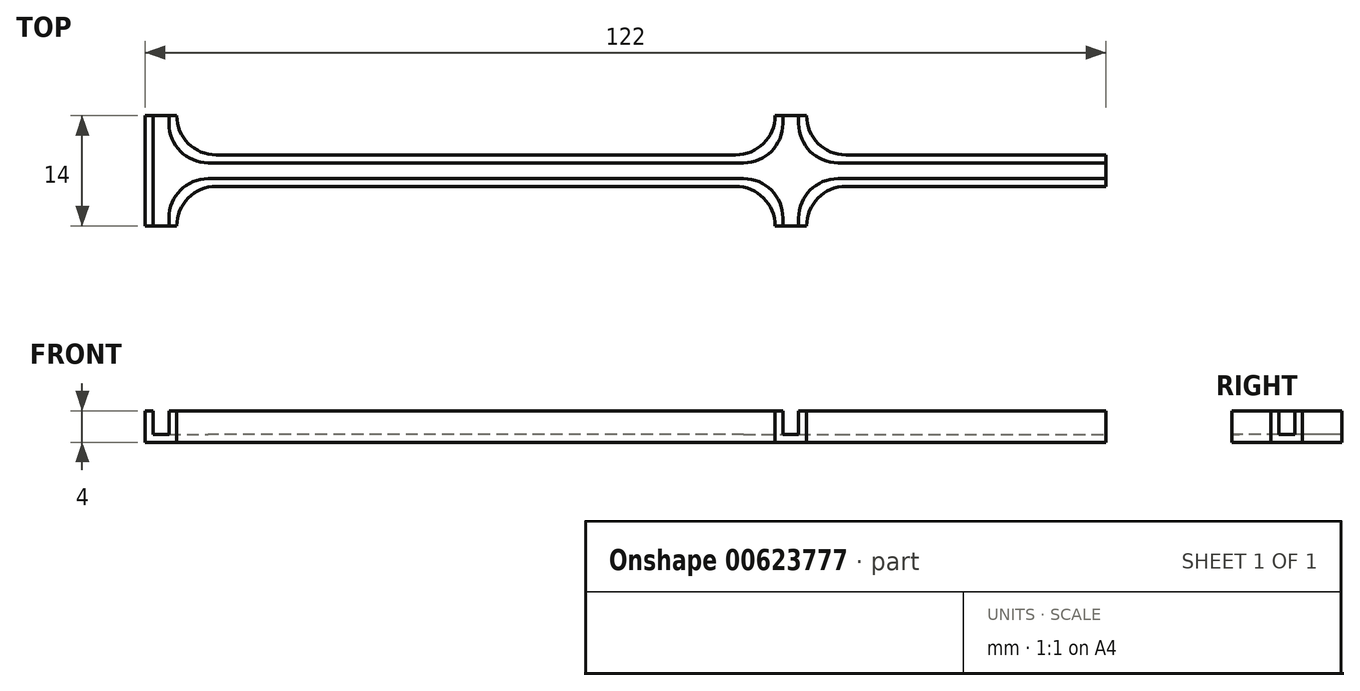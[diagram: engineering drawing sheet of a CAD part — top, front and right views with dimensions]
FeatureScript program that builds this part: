
annotation { "Feature Type Name" : "Feature", "Feature Type Description" : "" }
export const myFeature = defineFeature(function(context is Context, id is Id, definition is map)
    precondition{}
    {
        {
            var Q0;
            Q0=qCreatedBy(makeId("Top.planeOp"),FACE);
            var sketch = newSketch(context, id + "F0", { "sketchPlane" : qUnion([Q0])});
            skLineSegment(sketch, "E0.bottom", {"start": v(-61, 2) * mm, "end": v(61, 2) * mm});
            skLineSegment(sketch, "E0.top", {"start": v(-61, -2) * mm, "end": v(61, -2) * mm});
            skLineSegment(sketch, "E0.left", {"start": v(-61, 2) * mm, "end": v(-61, -2) * mm});
            skLineSegment(sketch, "E0.right", {"start": v(61, 2) * mm, "end": v(61, -2) * mm});
            skPoint(sketch, "E0.middle", {"position": v(0, 0) * mm});
            skLineSegment(sketch, "E1.bottom", {"start": v(-61, 7) * mm, "end": v(-57, 7) * mm});
            skLineSegment(sketch, "E1.top", {"start": v(-61, -7) * mm, "end": v(-57, -7) * mm});
            skLineSegment(sketch, "E1.left", {"start": v(-61, 7) * mm, "end": v(-61, -7) * mm});
            skLineSegment(sketch, "E1.right", {"start": v(-57, 7) * mm, "end": v(-57, -7) * mm});
            skLineSegment(sketch, "E2.bottom", {"start": v(-61, 0) * mm, "end": v(-61, 0) * mm});
            skLineSegment(sketch, "E2.top", {"start": v(-61, 0) * mm, "end": v(-61, 0) * mm});
            skLineSegment(sketch, "E2.left", {"start": v(-61, 0) * mm, "end": v(-61, 0) * mm});
            skLineSegment(sketch, "E2.right", {"start": v(-61, 0) * mm, "end": v(-61, 0) * mm});
            skLineSegment(sketch, "E3.bottom", {"start": v(19, 7) * mm, "end": v(23, 7) * mm});
            skLineSegment(sketch, "E3.top", {"start": v(19, -7) * mm, "end": v(23, -7) * mm});
            skLineSegment(sketch, "E3.left", {"start": v(23, 7) * mm, "end": v(23, -7) * mm});
            skLineSegment(sketch, "E3.right", {"start": v(19, 7) * mm, "end": v(19, -7) * mm});
            skLineSegment(sketch, "E4", {"start": v(-61, 0) * mm, "end": v(23, 0) * mm});
            skSolve(sketch);
        }
        {
            var Q0;
            {var subQ5=sQuery(id+"F0.wireOp",EDGE,"E1.bottom");Q0=makeQuery(id+"F0.imprint","IMPRINT",FACE,{"disambiguationData":[TD([[makeQuery(id+"F0.imprint","IMPRINT",EDGE,{"derivedFrom":subQ5}),-1.0]])]});}
            var Q1;
            {var subQ0=sQuery(id+"F0.wireOp",EDGE,"E1.right");var subQ1=sQuery(id+"F0.wireOp",EDGE,"E0.top");var subQ2=makeQuery(id+"F0.imprint","INTERSECT",VERTEX,{"derivedFrom":[subQ1,subQ0]});Q1=makeQuery(id+"F0.imprint","IMPRINT",FACE,{"disambiguationData":[TD([[makeQuery(id+"F0.imprint","IMPRINT",EDGE,{"disambiguationData":[TD([[subQ2,-1.0]])],"derivedFrom":subQ1}),1.0]])]});}
            var Q2;
            {var subQ0=sQuery(id+"F0.wireOp",EDGE,"E1.right");var subQ1=sQuery(id+"F0.wireOp",EDGE,"E0.bottom");var subQ2=makeQuery(id+"F0.imprint","INTERSECT",VERTEX,{"derivedFrom":[subQ1,subQ0]});Q2=makeQuery(id+"F0.imprint","IMPRINT",FACE,{"disambiguationData":[TD([[makeQuery(id+"F0.imprint","IMPRINT",EDGE,{"disambiguationData":[TD([[subQ2,-1.0]])],"derivedFrom":subQ1}),-1.0]])]});}
            var Q3;
            {var subQ0=sQuery(id+"F0.wireOp",EDGE,"E1.left");var subQ1=sQuery(id+"F0.wireOp",EDGE,"E0.top");var subQ2=makeQuery(id+"F0.imprint","INTERSECT",VERTEX,{"derivedFrom":[subQ1,subQ0]});Q3=makeQuery(id+"F0.imprint","IMPRINT",FACE,{"disambiguationData":[TD([[makeQuery(id+"F0.imprint","IMPRINT",EDGE,{"disambiguationData":[TD([[subQ2,-1.0]])],"derivedFrom":subQ1}),1.0]])]});}
            var Q4;
            {var subQ0=sQuery(id+"F0.wireOp",EDGE,"E1.left");var subQ1=sQuery(id+"F0.wireOp",EDGE,"E0.bottom");var subQ2=makeQuery(id+"F0.imprint","INTERSECT",VERTEX,{"derivedFrom":[subQ1,subQ0]});Q4=makeQuery(id+"F0.imprint","IMPRINT",FACE,{"disambiguationData":[TD([[makeQuery(id+"F0.imprint","IMPRINT",EDGE,{"disambiguationData":[TD([[subQ2,-1.0]])],"derivedFrom":subQ1}),-1.0]])]});}
            var Q5;
            {var subQ5=sQuery(id+"F0.wireOp",EDGE,"E1.top");Q5=makeQuery(id+"F0.imprint","IMPRINT",FACE,{"disambiguationData":[TD([[makeQuery(id+"F0.imprint","IMPRINT",EDGE,{"derivedFrom":subQ5}),1.0]])]});}
            var Q6;
            {var subQ4=sQuery(id+"F0.wireOp",EDGE,"E0.right");Q6=makeQuery(id+"F0.imprint","IMPRINT",FACE,{"disambiguationData":[TD([[makeQuery(id+"F0.imprint","IMPRINT",EDGE,{"derivedFrom":subQ4}),-1.0]])]});}
            var Q7;
            {var subQ0=sQuery(id+"F0.wireOp",EDGE,"E3.right");var subQ1=sQuery(id+"F0.wireOp",EDGE,"E0.bottom");var subQ2=makeQuery(id+"F0.imprint","INTERSECT",VERTEX,{"derivedFrom":[subQ1,subQ0]});Q7=makeQuery(id+"F0.imprint","IMPRINT",FACE,{"disambiguationData":[TD([[makeQuery(id+"F0.imprint","IMPRINT",EDGE,{"disambiguationData":[TD([[subQ2,-1.0]])],"derivedFrom":subQ1}),-1.0]])]});}
            var Q8;
            {var subQ0=sQuery(id+"F0.wireOp",EDGE,"E3.right");var subQ1=sQuery(id+"F0.wireOp",EDGE,"E0.top");var subQ2=makeQuery(id+"F0.imprint","INTERSECT",VERTEX,{"derivedFrom":[subQ1,subQ0]});Q8=makeQuery(id+"F0.imprint","IMPRINT",FACE,{"disambiguationData":[TD([[makeQuery(id+"F0.imprint","IMPRINT",EDGE,{"disambiguationData":[TD([[subQ2,-1.0]])],"derivedFrom":subQ1}),1.0]])]});}
            var Q9;
            {var subQ5=sQuery(id+"F0.wireOp",EDGE,"E3.bottom");Q9=makeQuery(id+"F0.imprint","IMPRINT",FACE,{"disambiguationData":[TD([[makeQuery(id+"F0.imprint","IMPRINT",EDGE,{"derivedFrom":subQ5}),-1.0]])]});}
            var Q10;
            {var subQ5=sQuery(id+"F0.wireOp",EDGE,"E3.top");Q10=makeQuery(id+"F0.imprint","IMPRINT",FACE,{"disambiguationData":[TD([[makeQuery(id+"F0.imprint","IMPRINT",EDGE,{"derivedFrom":subQ5}),1.0]])]});}
            extrude(context, id + "F1", {"entities" : qUnion([Q0, Q1, Q2, Q3, Q4, Q5, Q6, Q7, Q8, Q9, Q10]), "depth" : 1 * mm, "offsetDistance" : 25 * mm});
        }
        {
            var Q0;
            Q0=makeQuery(id+"F1.opExtrude","CAP_FACE",FACE,{"disambiguationData":[OSD([sQuery(id+"F0.wireOp",EDGE,"E0.bottom"),sQuery(id+"F0.wireOp",EDGE,"E0.top"),sQuery(id+"F0.wireOp",EDGE,"E0.right"),sQuery(id+"F0.wireOp",EDGE,"E1.bottom"),sQuery(id+"F0.wireOp",EDGE,"E1.top"),sQuery(id+"F0.wireOp",EDGE,"E1.left"),sQuery(id+"F0.wireOp",EDGE,"E1.right"),sQuery(id+"F0.wireOp",EDGE,"E3.bottom"),sQuery(id+"F0.wireOp",EDGE,"E3.top"),sQuery(id+"F0.wireOp",EDGE,"E3.left"),sQuery(id+"F0.wireOp",EDGE,"E3.right")])],"isStart":false});
            var sketch = newSketch(context, id + "F2", { "sketchPlane" : qUnion([Q0])});
            skLineSegment(sketch, "E5.bottom", {"start": v(-61, 7) * mm, "end": v(-60, 7) * mm});
            skLineSegment(sketch, "E5.top", {"start": v(-61, -7) * mm, "end": v(-60, -7) * mm});
            skLineSegment(sketch, "E5.left", {"start": v(-61, 7) * mm, "end": v(-61, -7) * mm});
            skLineSegment(sketch, "E5.right", {"start": v(-60, 7) * mm, "end": v(-60, -7) * mm});
            skLineSegment(sketch, "E6.bottom", {"start": v(-57, 7) * mm, "end": v(-58, 7) * mm});
            skLineSegment(sketch, "E6.top", {"start": v(-57, 1) * mm, "end": v(-58, 1) * mm});
            skLineSegment(sketch, "E6.left", {"start": v(-57, 7) * mm, "end": v(-57, 1) * mm});
            skLineSegment(sketch, "E6.right", {"start": v(-58, 7) * mm, "end": v(-58, 1) * mm});
            skLineSegment(sketch, "E7.bottom", {"start": v(-57, -7) * mm, "end": v(-58, -7) * mm});
            skLineSegment(sketch, "E7.top", {"start": v(-57, -1) * mm, "end": v(-58, -1) * mm});
            skLineSegment(sketch, "E7.left", {"start": v(-57, -7) * mm, "end": v(-57, -1) * mm});
            skLineSegment(sketch, "E7.right", {"start": v(-58, -7) * mm, "end": v(-58, -1) * mm});
            skLineSegment(sketch, "E8.bottom", {"start": v(-57, 2) * mm, "end": v(-51, 2) * mm});
            skLineSegment(sketch, "E8.top", {"start": v(-57, 1) * mm, "end": v(-51, 1) * mm});
            skLineSegment(sketch, "E8.left", {"start": v(-57, 2) * mm, "end": v(-57, 1) * mm});
            skLineSegment(sketch, "E8.right", {"start": v(-51, 2) * mm, "end": v(-51, 1) * mm});
            skLineSegment(sketch, "E9.bottom", {"start": v(-57, -1) * mm, "end": v(-51, -1) * mm});
            skLineSegment(sketch, "E9.top", {"start": v(-57, -2) * mm, "end": v(-51, -2) * mm});
            skLineSegment(sketch, "E9.left", {"start": v(-57, -1) * mm, "end": v(-57, -2) * mm});
            skLineSegment(sketch, "E9.right", {"start": v(-51, -1) * mm, "end": v(-51, -2) * mm});
            skLineSegment(sketch, "E10.bottom", {"start": v(19, 7) * mm, "end": v(20, 7) * mm});
            skLineSegment(sketch, "E10.top", {"start": v(19, 1) * mm, "end": v(20, 1) * mm});
            skLineSegment(sketch, "E10.left", {"start": v(19, 7) * mm, "end": v(19, 1) * mm});
            skLineSegment(sketch, "E10.right", {"start": v(20, 7) * mm, "end": v(20, 1) * mm});
            skLineSegment(sketch, "E11.bottom", {"start": v(19, -7) * mm, "end": v(20, -7) * mm});
            skLineSegment(sketch, "E11.top", {"start": v(19, -1) * mm, "end": v(20, -1) * mm});
            skLineSegment(sketch, "E11.left", {"start": v(19, -7) * mm, "end": v(19, -1) * mm});
            skLineSegment(sketch, "E11.right", {"start": v(20, -7) * mm, "end": v(20, -1) * mm});
            skLineSegment(sketch, "E12.bottom", {"start": v(23, -7) * mm, "end": v(22, -7) * mm});
            skLineSegment(sketch, "E12.top", {"start": v(23, -1) * mm, "end": v(22, -1) * mm});
            skLineSegment(sketch, "E12.left", {"start": v(23, -7) * mm, "end": v(23, -1) * mm});
            skLineSegment(sketch, "E12.right", {"start": v(22, -7) * mm, "end": v(22, -1) * mm});
            skLineSegment(sketch, "E13.bottom", {"start": v(23, 7) * mm, "end": v(22, 7) * mm});
            skLineSegment(sketch, "E13.top", {"start": v(23, 1) * mm, "end": v(22, 1) * mm});
            skLineSegment(sketch, "E13.left", {"start": v(23, 7) * mm, "end": v(23, 1) * mm});
            skLineSegment(sketch, "E13.right", {"start": v(22, 7) * mm, "end": v(22, 1) * mm});
            skLineSegment(sketch, "E14.bottom", {"start": v(23, 1) * mm, "end": v(28, 1) * mm});
            skLineSegment(sketch, "E14.top", {"start": v(23, 2) * mm, "end": v(28, 2) * mm});
            skLineSegment(sketch, "E14.left", {"start": v(23, 1) * mm, "end": v(23, 2) * mm});
            skLineSegment(sketch, "E14.right", {"start": v(28, 1) * mm, "end": v(28, 2) * mm});
            skLineSegment(sketch, "E15.bottom", {"start": v(23, -1) * mm, "end": v(28, -1) * mm});
            skLineSegment(sketch, "E15.top", {"start": v(23, -2) * mm, "end": v(28, -2) * mm});
            skLineSegment(sketch, "E15.left", {"start": v(23, -1) * mm, "end": v(23, -2) * mm});
            skLineSegment(sketch, "E15.right", {"start": v(28, -1) * mm, "end": v(28, -2) * mm});
            skLineSegment(sketch, "E16.bottom", {"start": v(19, -1) * mm, "end": v(14, -1) * mm});
            skLineSegment(sketch, "E16.top", {"start": v(19, -2) * mm, "end": v(14, -2) * mm});
            skLineSegment(sketch, "E16.left", {"start": v(19, -1) * mm, "end": v(19, -2) * mm});
            skLineSegment(sketch, "E16.right", {"start": v(14, -1) * mm, "end": v(14, -2) * mm});
            skLineSegment(sketch, "E17.bottom", {"start": v(19, 1) * mm, "end": v(14, 1) * mm});
            skLineSegment(sketch, "E17.top", {"start": v(19, 2) * mm, "end": v(14, 2) * mm});
            skLineSegment(sketch, "E17.left", {"start": v(19, 1) * mm, "end": v(19, 2) * mm});
            skLineSegment(sketch, "E17.right", {"start": v(14, 1) * mm, "end": v(14, 2) * mm});
            skLineSegment(sketch, "E18.bottom", {"start": v(-51, -1) * mm, "end": v(14, -1) * mm});
            skLineSegment(sketch, "E18.top", {"start": v(-51, -2) * mm, "end": v(14, -2) * mm});
            skLineSegment(sketch, "E19.bottom", {"start": v(-51, 2) * mm, "end": v(14, 2) * mm});
            skLineSegment(sketch, "E19.top", {"start": v(-51, 1) * mm, "end": v(14, 1) * mm});
            skLineSegment(sketch, "E19.right", {"start": v(14, 2) * mm, "end": v(14, 1) * mm});
            skLineSegment(sketch, "E20.bottom", {"start": v(28, 1) * mm, "end": v(61, 1) * mm});
            skLineSegment(sketch, "E20.top", {"start": v(28, 2) * mm, "end": v(61, 2) * mm});
            skLineSegment(sketch, "E20.right", {"start": v(61, 1) * mm, "end": v(61, 2) * mm});
            skLineSegment(sketch, "E21.bottom", {"start": v(28, -1) * mm, "end": v(61, -1) * mm});
            skLineSegment(sketch, "E21.top", {"start": v(28, -2) * mm, "end": v(61, -2) * mm});
            skLineSegment(sketch, "E21.right", {"start": v(61, -1) * mm, "end": v(61, -2) * mm});
            skSolve(sketch);
        }
        {
            var Q0;
            Q0=makeQuery(id+"F2.imprint","IMPRINT",FACE,{"disambiguationData":[TD([[makeQuery(id+"F2.imprint","IMPRINT",EDGE,{"derivedFrom":sQuery(id+"F2.wireOp",EDGE,"E5.bottom")}),-1.0]])]});
            var Q1;
            Q1=makeQuery(id+"F2.imprint","IMPRINT",FACE,{"disambiguationData":[TD([[makeQuery(id+"F2.imprint","IMPRINT",EDGE,{"derivedFrom":sQuery(id+"F2.wireOp",EDGE,"E6.bottom")}),-1.0]])]});
            var Q2;
            Q2=makeQuery(id+"F2.imprint","IMPRINT",FACE,{"disambiguationData":[TD([[makeQuery(id+"F2.imprint","IMPRINT",EDGE,{"derivedFrom":sQuery(id+"F2.wireOp",EDGE,"E8.bottom")}),-1.0]])]});
            var Q3;
            Q3=makeQuery(id+"F2.imprint","IMPRINT",FACE,{"disambiguationData":[TD([[makeQuery(id+"F2.imprint","IMPRINT",EDGE,{"derivedFrom":sQuery(id+"F2.wireOp",EDGE,"E9.bottom")}),-1.0]])]});
            var Q4;
            Q4=makeQuery(id+"F2.imprint","IMPRINT",FACE,{"disambiguationData":[TD([[makeQuery(id+"F2.imprint","IMPRINT",EDGE,{"derivedFrom":sQuery(id+"F2.wireOp",EDGE,"E7.bottom")}),1.0]])]});
            var Q5;
            Q5=makeQuery(id+"F2.imprint","IMPRINT",FACE,{"disambiguationData":[TD([[makeQuery(id+"F2.imprint","IMPRINT",EDGE,{"derivedFrom":sQuery(id+"F2.wireOp",EDGE,"E11.bottom")}),1.0]])]});
            var Q6;
            Q6=makeQuery(id+"F2.imprint","IMPRINT",FACE,{"disambiguationData":[TD([[makeQuery(id+"F2.imprint","IMPRINT",EDGE,{"derivedFrom":sQuery(id+"F2.wireOp",EDGE,"E10.bottom")}),-1.0]])]});
            var Q7;
            Q7=makeQuery(id+"F2.imprint","IMPRINT",FACE,{"disambiguationData":[TD([[makeQuery(id+"F2.imprint","IMPRINT",EDGE,{"derivedFrom":sQuery(id+"F2.wireOp",EDGE,"E17.bottom")}),-1.0]])]});
            var Q8;
            Q8=makeQuery(id+"F2.imprint","IMPRINT",FACE,{"disambiguationData":[TD([[makeQuery(id+"F2.imprint","IMPRINT",EDGE,{"derivedFrom":sQuery(id+"F2.wireOp",EDGE,"E16.bottom")}),1.0]])]});
            var Q9;
            Q9=makeQuery(id+"F2.imprint","IMPRINT",FACE,{"disambiguationData":[TD([[makeQuery(id+"F2.imprint","IMPRINT",EDGE,{"derivedFrom":sQuery(id+"F2.wireOp",EDGE,"E15.bottom")}),-1.0]])]});
            var Q10;
            Q10=makeQuery(id+"F2.imprint","IMPRINT",FACE,{"disambiguationData":[TD([[makeQuery(id+"F2.imprint","IMPRINT",EDGE,{"derivedFrom":sQuery(id+"F2.wireOp",EDGE,"E14.bottom")}),1.0]])]});
            var Q11;
            Q11=makeQuery(id+"F2.imprint","IMPRINT",FACE,{"disambiguationData":[TD([[makeQuery(id+"F2.imprint","IMPRINT",EDGE,{"derivedFrom":sQuery(id+"F2.wireOp",EDGE,"E13.bottom")}),-1.0]])]});
            var Q12;
            Q12=makeQuery(id+"F2.imprint","IMPRINT",FACE,{"disambiguationData":[TD([[makeQuery(id+"F2.imprint","IMPRINT",EDGE,{"derivedFrom":sQuery(id+"F2.wireOp",EDGE,"E12.bottom")}),1.0]])]});
            var Q13;
            Q13=makeQuery(id+"F2.imprint","IMPRINT",FACE,{"disambiguationData":[TD([[makeQuery(id+"F2.imprint","IMPRINT",EDGE,{"derivedFrom":sQuery(id+"F2.wireOp",EDGE,"E21.bottom")}),-1.0]])]});
            var Q14;
            Q14=makeQuery(id+"F2.imprint","IMPRINT",FACE,{"disambiguationData":[TD([[makeQuery(id+"F2.imprint","IMPRINT",EDGE,{"derivedFrom":sQuery(id+"F2.wireOp",EDGE,"E19.bottom")}),-1.0]])]});
            var Q15;
            Q15=makeQuery(id+"F2.imprint","IMPRINT",FACE,{"disambiguationData":[TD([[makeQuery(id+"F2.imprint","IMPRINT",EDGE,{"derivedFrom":sQuery(id+"F2.wireOp",EDGE,"E18.bottom")}),-1.0]])]});
            var Q16;
            Q16=makeQuery(id+"F2.imprint","IMPRINT",FACE,{"disambiguationData":[TD([[makeQuery(id+"F2.imprint","IMPRINT",EDGE,{"derivedFrom":sQuery(id+"F2.wireOp",EDGE,"E20.bottom")}),1.0]])]});
            extrude(context, id + "F3", {"entities" : qUnion([Q0, Q1, Q2, Q3, Q4, Q5, Q6, Q7, Q8, Q9, Q10, Q11, Q12, Q13, Q14, Q15, Q16]), "operationType" : NewBodyOperationType.ADD, "depth" : 3 * mm, "offsetDistance" : 25 * mm});
        }
        {
            var Q0;
            Q0=makeQuery(id+"F3.boolean.opBoolean","MERGE",EDGE,{"derivedFrom":[makeQuery(id+"F1.opExtrude","SWEPT_EDGE",EDGE,{"disambiguationData":[OSD([sQuery(id+"F0.wireOp",EDGE,"E0.top"),sQuery(id+"F0.wireOp",EDGE,"E3.left")])]}),makeQuery(id+"F3.opExtrude","SWEPT_EDGE",EDGE,{"disambiguationData":[OSD([sQuery(id+"F2.wireOp",EDGE,"E12.left"),sQuery(id+"F2.wireOp",EDGE,"E15.top"),sQuery(id+"F2.wireOp",EDGE,"E15.left")])]})]});
            var Q1;
            Q1=makeQuery(id+"F3.opExtrude","SWEPT_EDGE",EDGE,{"disambiguationData":[OSD([sQuery(id+"F2.wireOp",EDGE,"E11.top"),sQuery(id+"F2.wireOp",EDGE,"E11.right")])]});
            var Q2;
            Q2=makeQuery(id+"F3.opExtrude","SWEPT_EDGE",EDGE,{"disambiguationData":[OSD([sQuery(id+"F2.wireOp",EDGE,"E10.top"),sQuery(id+"F2.wireOp",EDGE,"E10.right")])]});
            var Q3;
            Q3=makeQuery(id+"F3.opExtrude","SWEPT_EDGE",EDGE,{"disambiguationData":[OSD([sQuery(id+"F2.wireOp",EDGE,"E13.top"),sQuery(id+"F2.wireOp",EDGE,"E13.right")])]});
            var Q4;
            Q4=makeQuery(id+"F3.boolean.opBoolean","MERGE",EDGE,{"derivedFrom":[makeQuery(id+"F1.opExtrude","SWEPT_EDGE",EDGE,{"disambiguationData":[OSD([sQuery(id+"F0.wireOp",EDGE,"E0.top"),sQuery(id+"F0.wireOp",EDGE,"E3.right")])]}),makeQuery(id+"F3.opExtrude","SWEPT_EDGE",EDGE,{"disambiguationData":[OSD([sQuery(id+"F2.wireOp",EDGE,"E11.left"),sQuery(id+"F2.wireOp",EDGE,"E16.top"),sQuery(id+"F2.wireOp",EDGE,"E16.left")])]})]});
            var Q5;
            Q5=makeQuery(id+"F3.opExtrude","SWEPT_EDGE",EDGE,{"disambiguationData":[OSD([sQuery(id+"F2.wireOp",EDGE,"E12.top"),sQuery(id+"F2.wireOp",EDGE,"E12.right")])]});
            var Q6;
            Q6=makeQuery(id+"F3.boolean.opBoolean","MERGE",EDGE,{"derivedFrom":[makeQuery(id+"F1.opExtrude","SWEPT_EDGE",EDGE,{"disambiguationData":[OSD([sQuery(id+"F0.wireOp",EDGE,"E0.bottom"),sQuery(id+"F0.wireOp",EDGE,"E3.right")])]}),makeQuery(id+"F3.opExtrude","SWEPT_EDGE",EDGE,{"disambiguationData":[OSD([sQuery(id+"F2.wireOp",EDGE,"E10.left"),sQuery(id+"F2.wireOp",EDGE,"E17.top"),sQuery(id+"F2.wireOp",EDGE,"E17.left")])]})]});
            var Q7;
            Q7=makeQuery(id+"F3.boolean.opBoolean","MERGE",EDGE,{"derivedFrom":[makeQuery(id+"F1.opExtrude","SWEPT_EDGE",EDGE,{"disambiguationData":[OSD([sQuery(id+"F0.wireOp",EDGE,"E0.bottom"),sQuery(id+"F0.wireOp",EDGE,"E3.left")])]}),makeQuery(id+"F3.opExtrude","SWEPT_EDGE",EDGE,{"disambiguationData":[OSD([sQuery(id+"F2.wireOp",EDGE,"E13.left"),sQuery(id+"F2.wireOp",EDGE,"E14.top"),sQuery(id+"F2.wireOp",EDGE,"E14.left")])]})]});
            fillet(context, id + "F4", {"entities" : qUnion([Q0, Q1, Q2, Q3, Q4, Q5, Q6, Q7]), "radius" : 5 * mm, "tangentPropagation" : true, "allowEdgeOverflow" : false});
        }
        {
            var Q0;
            Q0=makeQuery(id+"F3.boolean.opBoolean","MERGE",EDGE,{"derivedFrom":[makeQuery(id+"F1.opExtrude","SWEPT_EDGE",EDGE,{"disambiguationData":[OSD([sQuery(id+"F0.wireOp",EDGE,"E0.top"),sQuery(id+"F0.wireOp",EDGE,"E1.right")])]}),makeQuery(id+"F3.opExtrude","SWEPT_EDGE",EDGE,{"disambiguationData":[OSD([sQuery(id+"F2.wireOp",EDGE,"E7.left"),sQuery(id+"F2.wireOp",EDGE,"E9.top"),sQuery(id+"F2.wireOp",EDGE,"E9.left")])]})]});
            var Q1;
            Q1=makeQuery(id+"F3.opExtrude","SWEPT_EDGE",EDGE,{"disambiguationData":[OSD([sQuery(id+"F2.wireOp",EDGE,"E6.top"),sQuery(id+"F2.wireOp",EDGE,"E6.right")])]});
            var Q2;
            Q2=makeQuery(id+"F3.boolean.opBoolean","MERGE",EDGE,{"derivedFrom":[makeQuery(id+"F1.opExtrude","SWEPT_EDGE",EDGE,{"disambiguationData":[OSD([sQuery(id+"F0.wireOp",EDGE,"E0.bottom"),sQuery(id+"F0.wireOp",EDGE,"E1.right")])]}),makeQuery(id+"F3.opExtrude","SWEPT_EDGE",EDGE,{"disambiguationData":[OSD([sQuery(id+"F2.wireOp",EDGE,"E6.left"),sQuery(id+"F2.wireOp",EDGE,"E8.bottom"),sQuery(id+"F2.wireOp",EDGE,"E8.left")])]})]});
            var Q3;
            Q3=makeQuery(id+"F3.opExtrude","SWEPT_EDGE",EDGE,{"disambiguationData":[OSD([sQuery(id+"F2.wireOp",EDGE,"E7.top"),sQuery(id+"F2.wireOp",EDGE,"E7.right")])]});
            fillet(context, id + "F5", {"entities" : qUnion([Q0, Q1, Q2, Q3]), "radius" : 5 * mm, "tangentPropagation" : true, "allowEdgeOverflow" : false});
        }
    });
